# Revit family: CAROMA URBANE II 40MM BOTTLE TRAP
name_source: partatom
category: Plumbing Fixtures
units: mm (PartAtom-declared; Revit-internal decimal feet)

## family parameters
Cut with Voids When Loaded = Yes
Host = Face
OmniClass Number = 23.45.55.21
OmniClass Title = Drains (Wastes)
Part Type = Normal
Room Calculation Point = No
Round Connector Dimension = Use Diameter
Shared = No

## types (7) — shared parameters
Assembly Code = D2090500
CW Connection = No
Drop = 190 mm
DropCalc = 190 mm
FallAngle = 92.00°
FallCalc = 10 mm  [stored 0.0328084 ft]
FallLength = 300 mm
HW Connection = No
Manufacturer = GWA Bathrooms & Kitchens
Return = 300 mm
ReturnCalc = 300 mm
URL = https://www.caroma.com.au
Vent Connection = No
Waste Connection = Yes
zero-valued in all types: Default Elevation

## per-type parameters (varying)
| type | Material_Waste | Model |
| CAROMA URBANE II 40MM BOTTLE TRAP-CHROME | GWA_Metal-Chrome | 687295C |
| CAROMA URBANE II 40MM BOTTLE TRAP-MATTE BLACK | GWA-Metal-Black | 687294B |
| CAROMA URBANE II 40MM BOTTLE TRAP-BRUSHED BRASS | GWA_Metal-Brushed-Brass | 687294BB |
| CAROMA URBANE II 40MM BOTTLE TRAP-BRUSHED NICKEL | GWA_Metal-Brushed-Nickel | 687294BN |
| CAROMA URBANE II 40MM BOTTLE TRAP-GUNMETAL | GWA-Metal-Gunmetal Grey | 678294GM |
| CAROMA URBANE II 40MM BOTTLE TRAP-WHITE | GWA-Metal-White | 687294W |
| CAROMA URBANE II 40MM BOTTLE TRAP-BRUSHED BRONZE | GWA_Metal-Brushed-Bronze | 687294BBZ |

note: column(s) folded — value = type name in every type: Description

note: [stored X ft] marks values corroborated as IEEE doubles in the binary element streams (Revit-internal decimal feet)

## geometry (parser evidence)
native form markers: Sweep x2
no freeform markers — native parametric forms only
